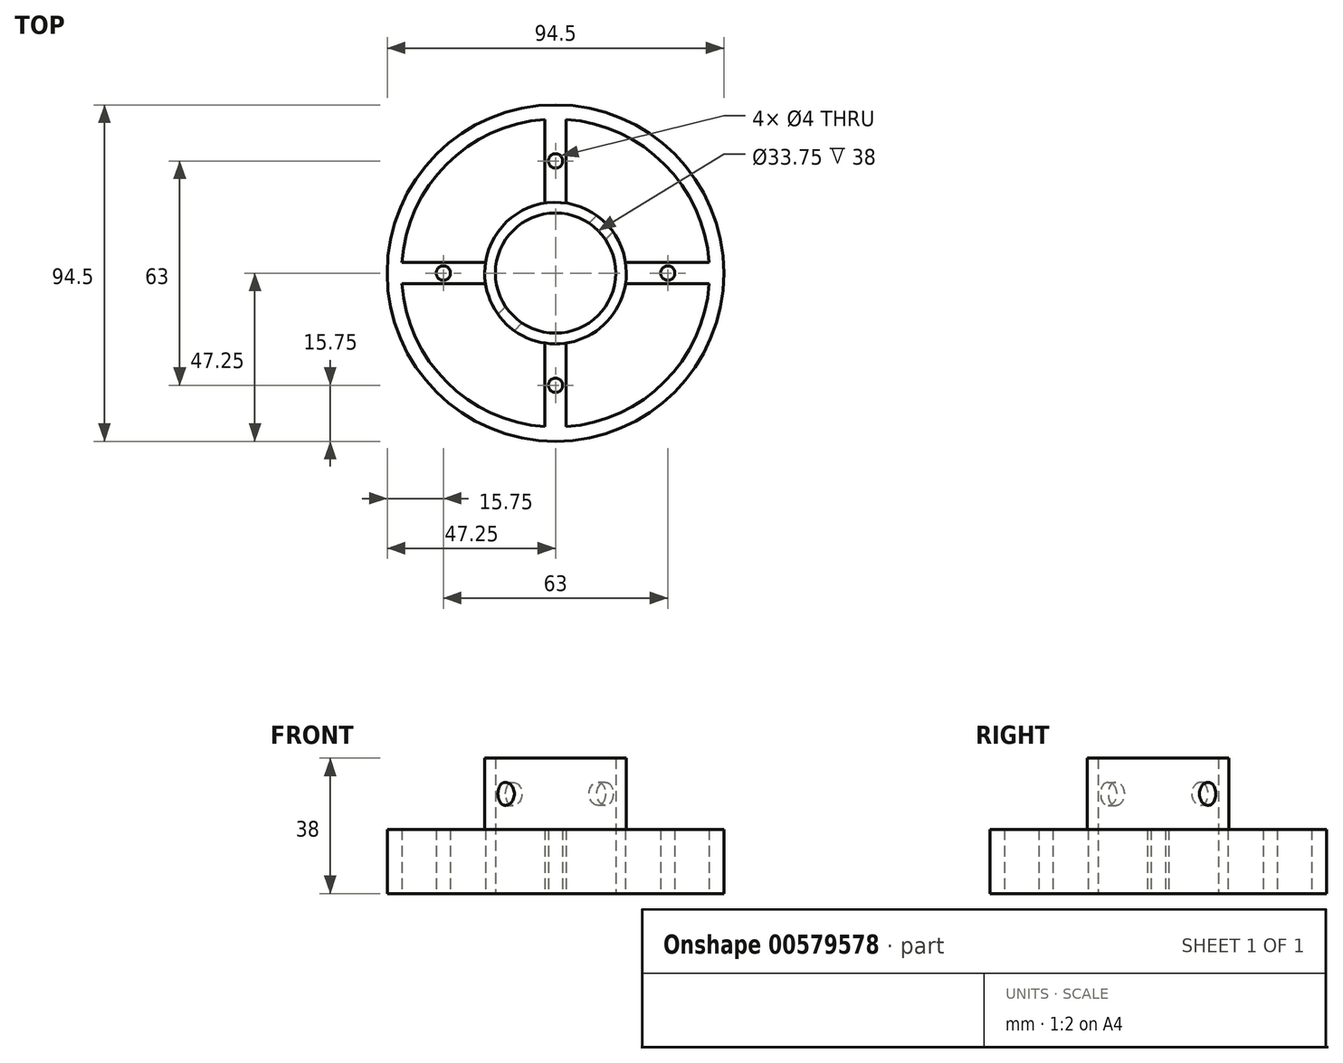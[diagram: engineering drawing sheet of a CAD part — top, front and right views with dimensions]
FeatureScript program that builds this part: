
annotation { "Feature Type Name" : "Feature", "Feature Type Description" : "" }
export const myFeature = defineFeature(function(context is Context, id is Id, definition is map)
    precondition{}
    {
        {
            var Q0;
            Q0=qCreatedBy(makeId("Top.planeOp"),FACE);
            var sketch = newSketch(context, id + "F0", { "sketchPlane" : qUnion([Q0])});
            skCircle(sketch, "E0", {"center": v(0, 0) * mm, "radius": 47.25 * mm});
            skCircle(sketch, "E1", {"center": v(0, 0) * mm, "radius": 16.88 * mm});
            skCircle(sketch, "E2", {"center": v(0, 0) * mm, "radius": 43.25 * mm});
            skLineSegment(sketch, "E3", {"start": v(-3, 0) * mm, "end": v(-3, 43.15) * mm});
            skLineSegment(sketch, "E4", {"start": v(3, 0) * mm, "end": v(3, 43.15) * mm});
            skLineSegment(sketch, "E5", {"start": v(-3, 0) * mm, "end": v(-3, -43.15) * mm});
            skLineSegment(sketch, "E6", {"start": v(3, 0) * mm, "end": v(3, -43.15) * mm});
            skLineSegment(sketch, "E7", {"start": v(0, 3) * mm, "end": v(43.15, 3) * mm});
            skLineSegment(sketch, "E8", {"start": v(0, -3) * mm, "end": v(43.15, -3) * mm});
            skLineSegment(sketch, "E9", {"start": v(0, 3) * mm, "end": v(-43.15, 3) * mm});
            skLineSegment(sketch, "E10", {"start": v(0, -3) * mm, "end": v(-43.15, -3) * mm});
            skCircle(sketch, "E11", {"center": v(0, 0) * mm, "radius": 19.88 * mm});
            skPoint(sketch, "E12", {"position": v(0, 31.5) * mm});
            skPoint(sketch, "E13", {"position": v(31.5, 0) * mm});
            skPoint(sketch, "E14", {"position": v(0, -31.5) * mm});
            skPoint(sketch, "E15", {"position": v(-31.5, 0) * mm});
            skCircle(sketch, "E16", {"center": v(0, 31.5) * mm, "radius": 2 * mm});
            skCircle(sketch, "E17", {"center": v(31.5, 0) * mm, "radius": 2 * mm});
            skCircle(sketch, "E18", {"center": v(0, -31.5) * mm, "radius": 2 * mm});
            skCircle(sketch, "E19", {"center": v(-31.5, 0) * mm, "radius": 2 * mm});
            skSolve(sketch);
        }
        {
            var Q0;
            {var subQ0=sQuery(id+"F0.wireOp",EDGE,"E4");var subQ1=sQuery(id+"F0.wireOp",EDGE,"E1");var subQ2=makeQuery(id+"F0.imprint","INTERSECT",VERTEX,{"derivedFrom":[subQ1,subQ0]});Q0=makeQuery(id+"F0.imprint","IMPRINT",FACE,{"disambiguationData":[TD([[makeQuery(id+"F0.imprint","IMPRINT",EDGE,{"disambiguationData":[TD([[subQ2,-1.0]])],"derivedFrom":subQ1}),-1.0]])]});}
            var Q1;
            {var subQ0=sQuery(id+"F0.wireOp",EDGE,"E7");var subQ1=sQuery(id+"F0.wireOp",EDGE,"E1");var subQ2=makeQuery(id+"F0.imprint","INTERSECT",VERTEX,{"derivedFrom":[subQ1,subQ0]});Q1=makeQuery(id+"F0.imprint","IMPRINT",FACE,{"disambiguationData":[TD([[makeQuery(id+"F0.imprint","IMPRINT",EDGE,{"disambiguationData":[TD([[subQ2,1.0]])],"derivedFrom":subQ1}),-1.0]])]});}
            var Q2;
            {var subQ0=sQuery(id+"F0.wireOp",EDGE,"E9");var subQ1=sQuery(id+"F0.wireOp",EDGE,"E1");var subQ2=makeQuery(id+"F0.imprint","INTERSECT",VERTEX,{"derivedFrom":[subQ1,subQ0]});Q2=makeQuery(id+"F0.imprint","IMPRINT",FACE,{"disambiguationData":[TD([[makeQuery(id+"F0.imprint","IMPRINT",EDGE,{"disambiguationData":[TD([[subQ2,-1.0]])],"derivedFrom":subQ1}),-1.0]])]});}
            var Q3;
            {var subQ0=sQuery(id+"F0.wireOp",EDGE,"E5");var subQ1=sQuery(id+"F0.wireOp",EDGE,"E1");var subQ2=makeQuery(id+"F0.imprint","INTERSECT",VERTEX,{"derivedFrom":[subQ1,subQ0]});Q3=makeQuery(id+"F0.imprint","IMPRINT",FACE,{"disambiguationData":[TD([[makeQuery(id+"F0.imprint","IMPRINT",EDGE,{"disambiguationData":[TD([[subQ2,-1.0]])],"derivedFrom":subQ1}),-1.0]])]});}
            var Q4;
            {var subQ0=sQuery(id+"F0.wireOp",EDGE,"E10");var subQ1=sQuery(id+"F0.wireOp",EDGE,"E1");var subQ2=makeQuery(id+"F0.imprint","INTERSECT",VERTEX,{"derivedFrom":[subQ1,subQ0]});Q4=makeQuery(id+"F0.imprint","IMPRINT",FACE,{"disambiguationData":[TD([[makeQuery(id+"F0.imprint","IMPRINT",EDGE,{"disambiguationData":[TD([[subQ2,-1.0]])],"derivedFrom":subQ1}),-1.0]])]});}
            var Q5;
            {var subQ0=sQuery(id+"F0.wireOp",EDGE,"E6");var subQ1=sQuery(id+"F0.wireOp",EDGE,"E1");var subQ2=makeQuery(id+"F0.imprint","INTERSECT",VERTEX,{"derivedFrom":[subQ1,subQ0]});Q5=makeQuery(id+"F0.imprint","IMPRINT",FACE,{"disambiguationData":[TD([[makeQuery(id+"F0.imprint","IMPRINT",EDGE,{"disambiguationData":[TD([[subQ2,-1.0]])],"derivedFrom":subQ1}),-1.0]])]});}
            var Q6;
            {var subQ0=sQuery(id+"F0.wireOp",EDGE,"E4");var subQ1=sQuery(id+"F0.wireOp",EDGE,"E1");var subQ2=makeQuery(id+"F0.imprint","INTERSECT",VERTEX,{"derivedFrom":[subQ1,subQ0]});Q6=makeQuery(id+"F0.imprint","IMPRINT",FACE,{"disambiguationData":[TD([[makeQuery(id+"F0.imprint","IMPRINT",EDGE,{"disambiguationData":[TD([[subQ2,1.0]])],"derivedFrom":subQ1}),-1.0]])]});}
            var Q7;
            {var subQ0=sQuery(id+"F0.wireOp",EDGE,"E3");var subQ1=sQuery(id+"F0.wireOp",EDGE,"E1");var subQ2=makeQuery(id+"F0.imprint","INTERSECT",VERTEX,{"derivedFrom":[subQ1,subQ0]});Q7=makeQuery(id+"F0.imprint","IMPRINT",FACE,{"disambiguationData":[TD([[makeQuery(id+"F0.imprint","IMPRINT",EDGE,{"disambiguationData":[TD([[subQ2,-1.0]])],"derivedFrom":subQ1}),-1.0]])]});}
            var Q8;
            {var subQ0=sQuery(id+"F0.wireOp",EDGE,"E7");var subQ1=sQuery(id+"F0.wireOp",EDGE,"E2");var subQ2=makeQuery(id+"F0.imprint","INTERSECT",VERTEX,{"derivedFrom":[subQ1,subQ0]});Q8=makeQuery(id+"F0.imprint","IMPRINT",FACE,{"disambiguationData":[TD([[makeQuery(id+"F0.imprint","IMPRINT",EDGE,{"disambiguationData":[TD([[subQ2,1.0]])],"derivedFrom":subQ1}),1.0]])]});}
            var Q9;
            {var subQ0=sQuery(id+"F0.wireOp",EDGE,"E9");var subQ1=sQuery(id+"F0.wireOp",EDGE,"E2");var subQ2=makeQuery(id+"F0.imprint","INTERSECT",VERTEX,{"derivedFrom":[subQ1,subQ0]});Q9=makeQuery(id+"F0.imprint","IMPRINT",FACE,{"disambiguationData":[TD([[makeQuery(id+"F0.imprint","IMPRINT",EDGE,{"disambiguationData":[TD([[subQ2,-1.0]])],"derivedFrom":subQ1}),1.0]])]});}
            var Q10;
            {var subQ0=sQuery(id+"F0.wireOp",EDGE,"E3");var subQ1=sQuery(id+"F0.wireOp",EDGE,"E2");var subQ2=makeQuery(id+"F0.imprint","INTERSECT",VERTEX,{"derivedFrom":[subQ1,subQ0]});Q10=makeQuery(id+"F0.imprint","IMPRINT",FACE,{"disambiguationData":[TD([[makeQuery(id+"F0.imprint","IMPRINT",EDGE,{"disambiguationData":[TD([[subQ2,1.0]])],"derivedFrom":subQ1}),1.0]])]});}
            var Q11;
            {var subQ0=sQuery(id+"F0.wireOp",EDGE,"E5");var subQ1=sQuery(id+"F0.wireOp",EDGE,"E2");var subQ2=makeQuery(id+"F0.imprint","INTERSECT",VERTEX,{"derivedFrom":[subQ1,subQ0]});Q11=makeQuery(id+"F0.imprint","IMPRINT",FACE,{"disambiguationData":[TD([[makeQuery(id+"F0.imprint","IMPRINT",EDGE,{"disambiguationData":[TD([[subQ2,-1.0]])],"derivedFrom":subQ1}),1.0]])]});}
            var Q12;
            Q12=makeQuery(id+"F0.imprint","IMPRINT",FACE,{"disambiguationData":[TD([[makeQuery(id+"F0.imprint","IMPRINT",EDGE,{"derivedFrom":sQuery(id+"F0.wireOp",EDGE,"E0")}),1.0]])]});
            extrude(context, id + "F1", {"entities" : qUnion([Q0, Q1, Q2, Q3, Q4, Q5, Q6, Q7, Q8, Q9, Q10, Q11, Q12]), "depth" : 18 * mm, "offsetDistance" : 25 * mm});
        }
        {
            var Q0;
            Q0=makeQuery(id+"F1.opExtrude","CAP_FACE",FACE,{"disambiguationData":[OSD([sQuery(id+"F0.wireOp",EDGE,"E0"),sQuery(id+"F0.wireOp",EDGE,"E1"),sQuery(id+"F0.wireOp",EDGE,"E2"),sQuery(id+"F0.wireOp",EDGE,"E3"),sQuery(id+"F0.wireOp",EDGE,"E4"),sQuery(id+"F0.wireOp",EDGE,"E5"),sQuery(id+"F0.wireOp",EDGE,"E6"),sQuery(id+"F0.wireOp",EDGE,"E7"),sQuery(id+"F0.wireOp",EDGE,"E8"),sQuery(id+"F0.wireOp",EDGE,"E9"),sQuery(id+"F0.wireOp",EDGE,"E10"),sQuery(id+"F0.wireOp",EDGE,"E11"),sQuery(id+"F0.wireOp",EDGE,"E16"),sQuery(id+"F0.wireOp",EDGE,"E17"),sQuery(id+"F0.wireOp",EDGE,"E18"),sQuery(id+"F0.wireOp",EDGE,"E19")])],"isStart":false});
            var sketch = newSketch(context, id + "F2", { "sketchPlane" : qUnion([Q0])});
            skCircle(sketch, "E20", {"center": v(0, 0) * mm, "radius": 16.88 * mm});
            skCircle(sketch, "E21", {"center": v(0, 0) * mm, "radius": 19.88 * mm});
            skSolve(sketch);
        }
        {
            var Q0;
            Q0=makeQuery(id+"F2.imprint","IMPRINT",FACE,{"disambiguationData":[TD([[makeQuery(id+"F2.imprint","IMPRINT",EDGE,{"derivedFrom":sQuery(id+"F2.wireOp",EDGE,"E20")}),-1.0]])]});
            extrude(context, id + "F3", {"entities" : qUnion([Q0]), "operationType" : NewBodyOperationType.ADD, "depth" : 20 * mm, "offsetDistance" : 25 * mm});
        }
        {
            var Q0;
            Q0=qCreatedBy(makeId("Right.planeOp"),FACE);
            var sketch = newSketch(context, id + "F4", { "sketchPlane" : qUnion([Q0])});
            skCircle(sketch, "E22", {"center": v(0, 28) * mm, "radius": 3.5 * mm});
            skSolve(sketch);
        }
        {
            var Q0;
            Q0=qCreatedBy(makeId("Front.planeOp"),FACE);
            var sketch = newSketch(context, id + "F5", { "sketchPlane" : qUnion([Q0])});
            skLineSegment(sketch, "E23", {"start": v(0, 0) * mm, "end": v(0, 70.09) * mm, "construction": true});
            skSolve(sketch);
        }
        {
            var Q0;
            Q0=sQuery(id+"F5.wireOp",EDGE,"E23");
            cPlane(context, id + "F6", {"entities" : qUnion([Q0]), "cplaneType" : CPlaneType.LINE_ANGLE, "offset" : 25 * mm, "angle" : 45 * degree, "width" : 150 * mm, "height" : 150 * mm});
        }
        {
            var Q0;
            Q0=qCreatedBy(id+"F6.planeOp",FACE);
            var sketch = newSketch(context, id + "F7", { "sketchPlane" : qUnion([Q0])});
            skCircle(sketch, "E24", {"center": v(0, 28) * mm, "radius": 3.25 * mm});
            skSolve(sketch);
        }
        {
            var Q0;
            Q0=makeQuery(id+"F7.imprint","IMPRINT",FACE,{"disambiguationData":[TD([[makeQuery(id+"F7.imprint","IMPRINT",EDGE,{"derivedFrom":sQuery(id+"F7.wireOp",EDGE,"E24")}),1.0]])]});
            extrude(context, id + "F8", {"entities" : qUnion([Q0]), "operationType" : NewBodyOperationType.REMOVE, "oppositeDirection" : true, "depth" : 25 * mm, "offsetDistance" : 25 * mm});
        }
        {
            var Q0;
            Q0=makeQuery(id+"F7.imprint","IMPRINT",FACE,{"disambiguationData":[TD([[makeQuery(id+"F7.imprint","IMPRINT",EDGE,{"derivedFrom":sQuery(id+"F7.wireOp",EDGE,"E24")}),1.0]])]});
            extrude(context, id + "F9", {"entities" : qUnion([Q0]), "operationType" : NewBodyOperationType.REMOVE, "depth" : 25 * mm, "offsetDistance" : 25 * mm});
        }
    });
